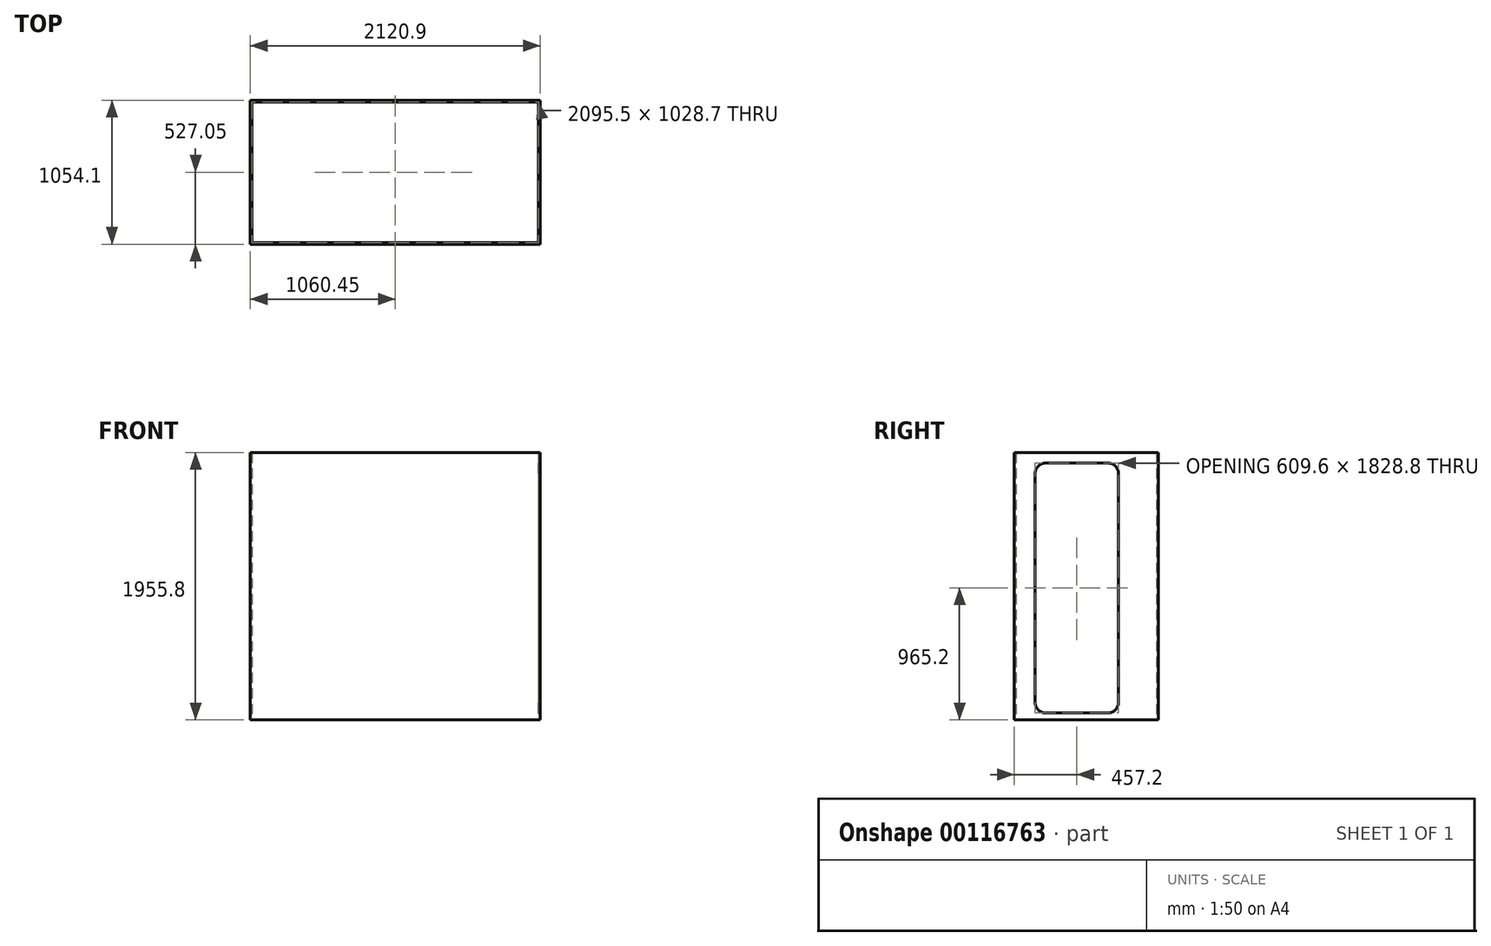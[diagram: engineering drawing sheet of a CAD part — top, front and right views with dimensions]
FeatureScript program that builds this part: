
annotation { "Feature Type Name" : "Feature", "Feature Type Description" : "" }
export const myFeature = defineFeature(function(context is Context, id is Id, definition is map)
    precondition{}
    {
        {
            var Q0;
            Q0=qCreatedBy(makeId("Top.planeOp"),FACE);
            var sketch = newSketch(context, id + "F0", { "sketchPlane" : qUnion([Q0])});
            skLineSegment(sketch, "E0.bottom", {"start": v(0, 0) * mm, "end": v(2120.9, 0) * mm});
            skLineSegment(sketch, "E0.top", {"start": v(0, 1054.1) * mm, "end": v(2120.9, 1054.1) * mm});
            skLineSegment(sketch, "E0.left", {"start": v(0, 0) * mm, "end": v(0, 1054.1) * mm});
            skLineSegment(sketch, "E0.right", {"start": v(2120.9, 0) * mm, "end": v(2120.9, 1054.1) * mm});
            skLineSegment(sketch, "E1.bottom", {"start": v(2108.2, 12.7) * mm, "end": v(12.7, 12.7) * mm});
            skLineSegment(sketch, "E1.top", {"start": v(2108.2, 1041.4) * mm, "end": v(12.7, 1041.4) * mm});
            skLineSegment(sketch, "E1.left", {"start": v(2108.2, 12.7) * mm, "end": v(2108.2, 1041.4) * mm});
            skLineSegment(sketch, "E1.right", {"start": v(12.7, 12.7) * mm, "end": v(12.7, 1041.4) * mm});
            skPoint(sketch, "E1.middle", {"position": v(1060.45, 527.05) * mm});
            skPoint(sketch, "E1.middle.positionSnap0", {"position": v(1060.45, 1054.1) * mm});
            skPoint(sketch, "E1.centerSnap0", {"position": v(1060.45, 1054.1) * mm});
            skSolve(sketch);
        }
        {
            var Q0;
            Q0 = qSketchRegion(id + "F0", true);
            extrude(context, id + "F1", {"entities" : qUnion([Q0]), "depth" : 1955.8 * mm});
        }
        {
            var Q0;
            Q0=makeQuery(id+"F1.opExtrude","SWEPT_FACE",FACE,{"disambiguationData":[OSD([sQuery(id+"F0.wireOp",EDGE,"E0.right")])]});
            var sketch = newSketch(context, id + "F2", { "sketchPlane" : qUnion([Q0])});
            skLineSegment(sketch, "E2", {"start": v(0, 0) * mm, "end": v(1054.1, 0) * mm});
            skLineSegment(sketch, "E3", {"start": v(0, 0) * mm, "end": v(152.4, 0) * mm});
            skLineSegment(sketch, "E4", {"start": v(152.4, 0) * mm, "end": v(152.4, 50.8) * mm});
            skLineSegment(sketch, "E5", {"start": v(228.6, 50.8) * mm, "end": v(685.8, 50.8) * mm});
            skLineSegment(sketch, "E6", {"start": v(762, 127) * mm, "end": v(762, 1803.4) * mm});
            skLineSegment(sketch, "E7", {"start": v(685.8, 1879.6) * mm, "end": v(228.6, 1879.6) * mm});
            skLineSegment(sketch, "E8", {"start": v(152.4, 1803.4) * mm, "end": v(152.4, 127) * mm});
            skPoint(sketch, "E9.visualSharp", {"position": v(152.4, 1879.6) * mm});
            skArc(sketch, "E9.filletArc", {"start": v(228.6, 1879.6) * mm, "mid": v(174.72, 1857.28) * mm, "end": v(152.4, 1803.4) * mm});
            skPoint(sketch, "E10.visualSharp", {"position": v(762, 1879.6) * mm});
            skArc(sketch, "E10.filletArc", {"start": v(762, 1803.4) * mm, "mid": v(739.68, 1857.28) * mm, "end": v(685.8, 1879.6) * mm});
            skPoint(sketch, "E11.visualSharp", {"position": v(152.4, 50.8) * mm});
            skArc(sketch, "E11.filletArc", {"start": v(152.4, 127) * mm, "mid": v(174.72, 73.12) * mm, "end": v(228.6, 50.8) * mm});
            skPoint(sketch, "E12.visualSharp", {"position": v(762, 50.8) * mm});
            skArc(sketch, "E12.filletArc", {"start": v(685.8, 50.8) * mm, "mid": v(739.68, 73.12) * mm, "end": v(762, 127) * mm});
            skSolve(sketch);
        }
        {
            var Q0;
            Q0 = qSketchRegion(id + "F2", true);
            extrude(context, id + "F3", {"entities" : qUnion([Q0]), "operationType" : NewBodyOperationType.REMOVE, "endBound" : BoundingType.UP_TO_NEXT, "oppositeDirection" : true, "depth" : 25.4 * mm});
        }
    });
